# Revit family: TV-201-C
name_source: partatom
category: Aparatos sanitarios
units: mm (PartAtom-declared; Revit-internal decimal feet)

## family parameters
Compartido = No
Corte con vacíos al cargar = No
Cota de conector redondo = Diámetro de uso
Número OmniClass = 23.45.00.00
Punto de cálculo de habitación = No
Se basa en plano de trabajo = No
Siempre vertical = Sí
Tipo de pieza = Normal
Título OmniClass = Sanitary, Laundry, and Cleaning Equipment

## types (1)
- TV-201
    Batteries = Works With a DL-223 (Duracell) Lithium Battery Or CR-P2 (Panasonic)
    Certification = http://www.helvex.com.mx
    Chrome = BrassChromed
    Comentarios de tipo = Electronic Line
    Conexión AF = No
    Connection = ½" - 14 NPSM
    Descripción = Electronic Faucet to Swivel Wall Lavatory Battery
    Detection Range = 1.9" (50 mm) - 9.4" (240 mm)
    Documentation = http://www.helvex.com.mx
    Elevación por defecto = 0"
    Fabricante = HELVEX
    Features = Infrared Sensor, Filter With Check Valve For Maintenance, Swivel Outlet
    Feeding Voltage = 6 V
    Instructive = http://www.helvex.com.mx
    Max. Working Pressure = 85.3 psi
    Min. Working Pressure = 5.7 psi
    Modelo = TV-201
    URL = http://www.helvex.com.mx

## geometry (parser evidence)
native form markers: Sweep x3
no freeform markers — native parametric forms only
